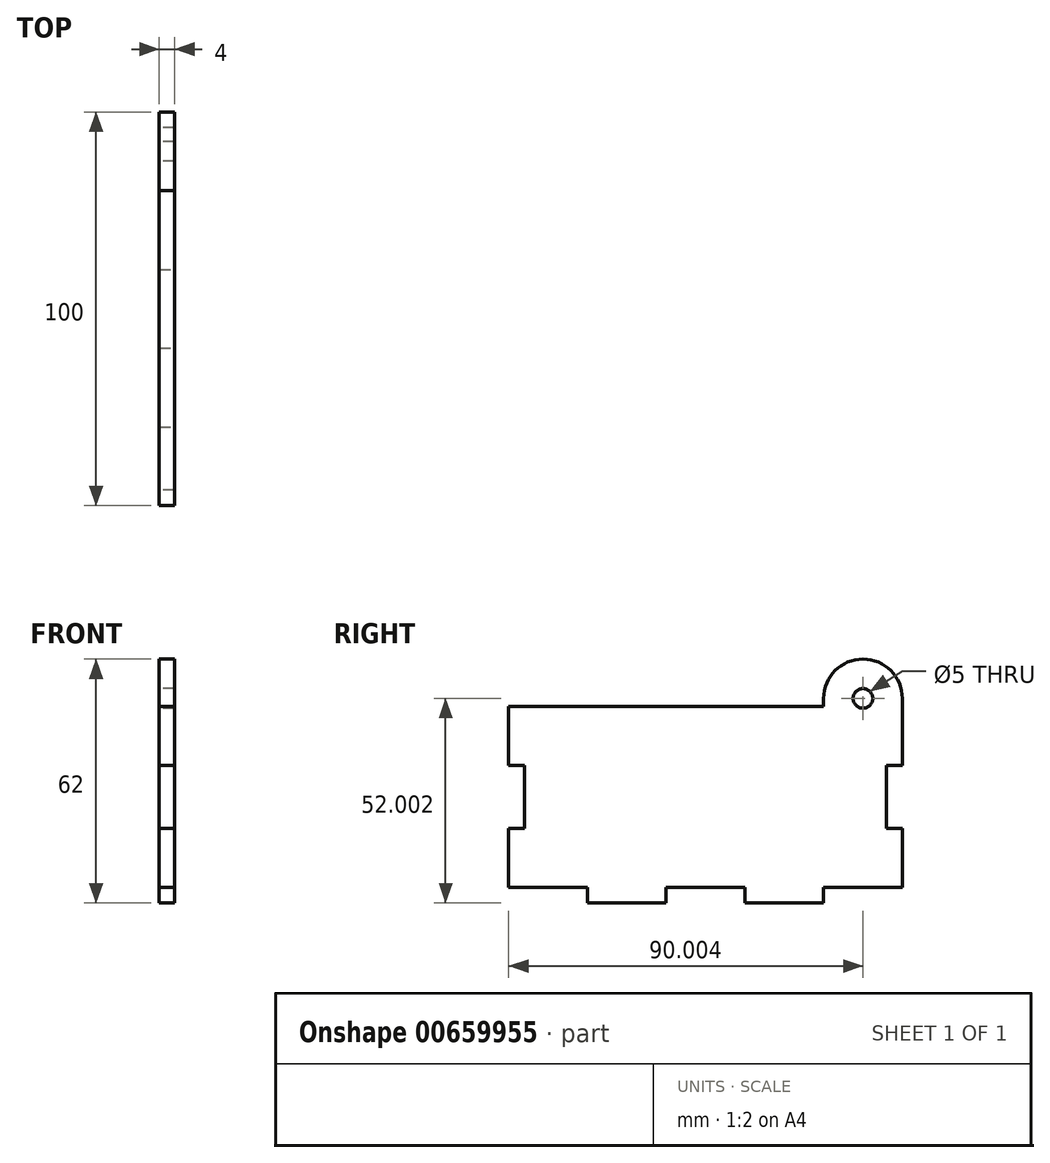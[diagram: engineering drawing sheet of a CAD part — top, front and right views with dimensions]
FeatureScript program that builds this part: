
annotation { "Feature Type Name" : "Feature", "Feature Type Description" : "" }
export const myFeature = defineFeature(function(context is Context, id is Id, definition is map)
    precondition{}
    {
        {
            var Q0;
            Q0=qCreatedBy(makeId("Right.planeOp"),FACE);
            var sketch = newSketch(context, id + "F0", { "sketchPlane" : qUnion([Q0])});
            skLineSegment(sketch, "E0.bottom", {"start": v(-101.44, 45.96) * mm, "end": v(-21.44, 45.96) * mm});
            skLineSegment(sketch, "E0.top", {"start": v(-101.44, -4.04) * mm, "end": v(-1.44, -4.04) * mm});
            skLineSegment(sketch, "E0.left", {"start": v(-101.44, 45.96) * mm, "end": v(-101.44, -4.04) * mm});
            skLineSegment(sketch, "E0.right", {"start": v(-1.44, 45.96) * mm, "end": v(-1.44, -4.04) * mm});
            skLineSegment(sketch, "E1.bottom", {"start": v(-101.44, 30.96) * mm, "end": v(-97.44, 30.96) * mm});
            skLineSegment(sketch, "E1.top", {"start": v(-101.44, 14.96) * mm, "end": v(-97.44, 14.96) * mm});
            skLineSegment(sketch, "E1.left", {"start": v(-101.44, 30.96) * mm, "end": v(-101.44, 14.96) * mm});
            skLineSegment(sketch, "E1.right", {"start": v(-97.44, 30.96) * mm, "end": v(-97.44, 14.96) * mm});
            skLineSegment(sketch, "E2.bottom", {"start": v(-1.44, 30.96) * mm, "end": v(-5.44, 30.96) * mm});
            skLineSegment(sketch, "E2.top", {"start": v(-1.44, 14.96) * mm, "end": v(-5.44, 14.96) * mm});
            skLineSegment(sketch, "E2.left", {"start": v(-1.44, 30.96) * mm, "end": v(-1.44, 14.96) * mm});
            skLineSegment(sketch, "E2.right", {"start": v(-5.44, 30.96) * mm, "end": v(-5.44, 14.96) * mm});
            skLineSegment(sketch, "E3.left", {"start": v(-1.44, 45.96) * mm, "end": v(-1.44, 47.96) * mm});
            skLineSegment(sketch, "E3.right", {"start": v(-21.44, 45.96) * mm, "end": v(-21.44, 47.96) * mm});
            skArc(sketch, "E4", {"start": v(-1.44, 47.96) * mm, "mid": v(-11.44, 57.96) * mm, "end": v(-21.44, 47.96) * mm});
            skCircle(sketch, "E5", {"center": v(-11.44, 47.96) * mm, "radius": 2.5 * mm});
            skSolve(sketch);
        }
        {
            var Q0;
            {var subQ7=sQuery(id+"F0.wireOp",EDGE,"E0.bottom");Q0=makeQuery(id+"F0.imprint","IMPRINT",FACE,{"disambiguationData":[TD([[makeQuery(id+"F0.imprint","IMPRINT",EDGE,{"derivedFrom":subQ7}),-1.0]])]});}
            extrude(context, id + "F1", {"entities" : qUnion([Q0]), "depth" : 4 * mm, "offsetDistance" : 25 * mm});
        }
        {
            var Q0;
            Q0=makeQuery(id+"F1.opExtrude","CAP_FACE",FACE,{"disambiguationData":[OSD([sQuery(id+"F0.wireOp",EDGE,"E0.bottom"),sQuery(id+"F0.wireOp",EDGE,"E0.top"),sQuery(id+"F0.wireOp",EDGE,"E0.left"),sQuery(id+"F0.wireOp",EDGE,"E0.right"),sQuery(id+"F0.wireOp",EDGE,"E1.bottom"),sQuery(id+"F0.wireOp",EDGE,"E1.top"),sQuery(id+"F0.wireOp",EDGE,"E1.right"),sQuery(id+"F0.wireOp",EDGE,"E2.bottom"),sQuery(id+"F0.wireOp",EDGE,"E2.top"),sQuery(id+"F0.wireOp",EDGE,"E2.right"),sQuery(id+"F0.wireOp",EDGE,"E3.left"),sQuery(id+"F0.wireOp",EDGE,"E3.right"),sQuery(id+"F0.wireOp",EDGE,"E4"),sQuery(id+"F0.wireOp",EDGE,"E5")])],"isStart":false});
            var sketch = newSketch(context, id + "F2", { "sketchPlane" : qUnion([Q0])});
            skLineSegment(sketch, "E6.bottom", {"start": v(-101.44, -4.04) * mm, "end": v(-81.44, -4.04) * mm});
            skLineSegment(sketch, "E6.top", {"start": v(-101.44, -0.04) * mm, "end": v(-81.44, -0.04) * mm});
            skLineSegment(sketch, "E6.left", {"start": v(-101.44, -4.04) * mm, "end": v(-101.44, -0.04) * mm});
            skLineSegment(sketch, "E6.right", {"start": v(-81.44, -4.04) * mm, "end": v(-81.44, -0.04) * mm});
            skLineSegment(sketch, "E7.bottom", {"start": v(-61.44, -4.04) * mm, "end": v(-41.44, -4.04) * mm});
            skLineSegment(sketch, "E7.top", {"start": v(-61.44, -0.04) * mm, "end": v(-41.44, -0.04) * mm});
            skLineSegment(sketch, "E7.left", {"start": v(-61.44, -4.04) * mm, "end": v(-61.44, -0.04) * mm});
            skLineSegment(sketch, "E7.right", {"start": v(-41.44, -4.04) * mm, "end": v(-41.44, -0.04) * mm});
            skLineSegment(sketch, "E8.bottom", {"start": v(-1.44, -4.04) * mm, "end": v(-21.44, -4.04) * mm});
            skLineSegment(sketch, "E8.top", {"start": v(-1.44, -0.04) * mm, "end": v(-21.44, -0.04) * mm});
            skLineSegment(sketch, "E8.left", {"start": v(-1.44, -4.04) * mm, "end": v(-1.44, -0.04) * mm});
            skLineSegment(sketch, "E8.right", {"start": v(-21.44, -4.04) * mm, "end": v(-21.44, -0.04) * mm});
            skSolve(sketch);
        }
        {
            var Q0;
            Q0 = qSketchRegion(id + "F2", true);
            extrude(context, id + "F3", {"entities" : qUnion([Q0]), "operationType" : NewBodyOperationType.REMOVE, "oppositeDirection" : true, "depth" : 4 * mm, "offsetDistance" : 25 * mm});
        }
    });
